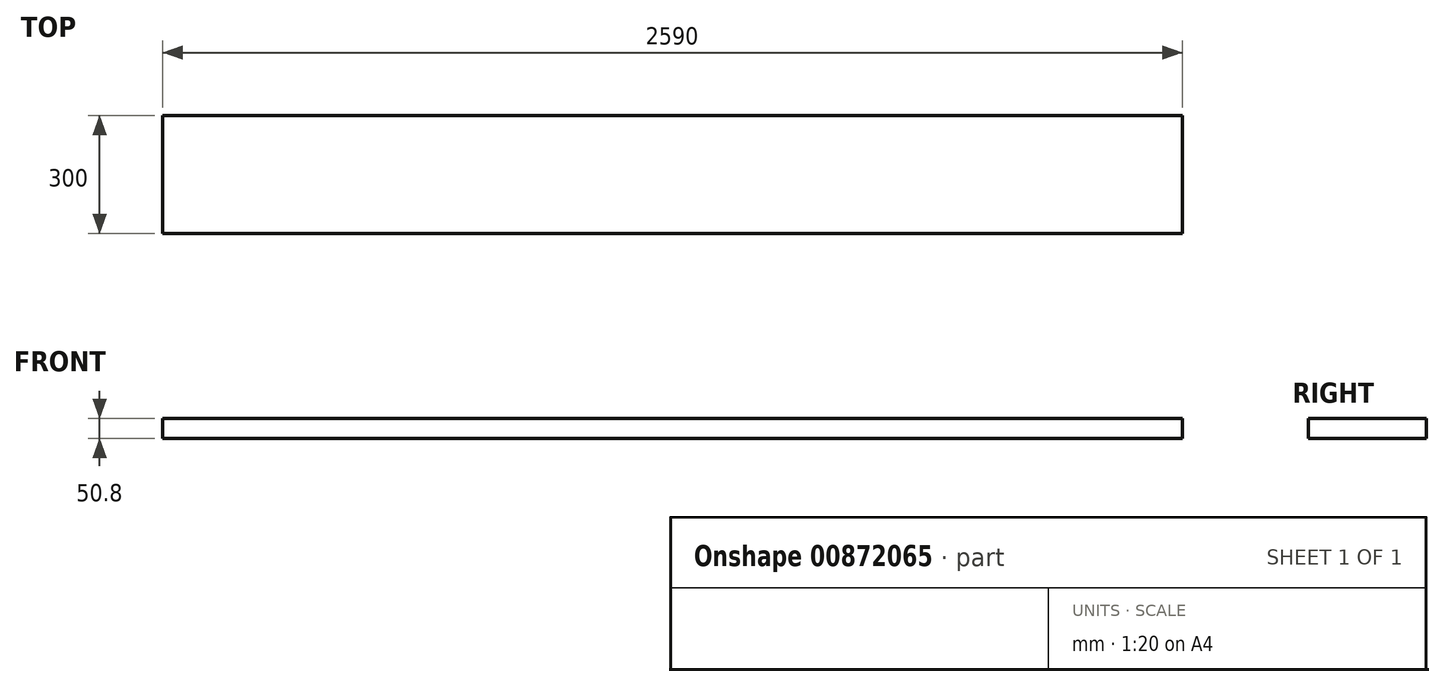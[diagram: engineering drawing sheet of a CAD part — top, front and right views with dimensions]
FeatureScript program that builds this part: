
annotation { "Feature Type Name" : "Feature", "Feature Type Description" : "" }
export const myFeature = defineFeature(function(context is Context, id is Id, definition is map)
    precondition{}
    {
        {
            var Q0;
            Q0=qCreatedBy(makeId("Top.planeOp"),FACE);
            var sketch = newSketch(context, id + "F0", { "sketchPlane" : qUnion([Q0])});
            skLineSegment(sketch, "E0.bottom", {"start": v(0, 0) * mm, "end": v(2590, 0) * mm});
            skLineSegment(sketch, "E0.top", {"start": v(0, 300) * mm, "end": v(2590, 300) * mm});
            skLineSegment(sketch, "E0.left", {"start": v(0, 0) * mm, "end": v(0, 300) * mm});
            skLineSegment(sketch, "E0.right", {"start": v(2590, 0) * mm, "end": v(2590, 300) * mm});
            skSolve(sketch);
        }
        {
            var Q0;
            Q0 = qSketchRegion(id + "F0", true);
            extrude(context, id + "F1", {"entities" : qUnion([Q0]), "depth" : 50.8 * mm, "offsetDistance" : 25 * mm});
        }
    });
